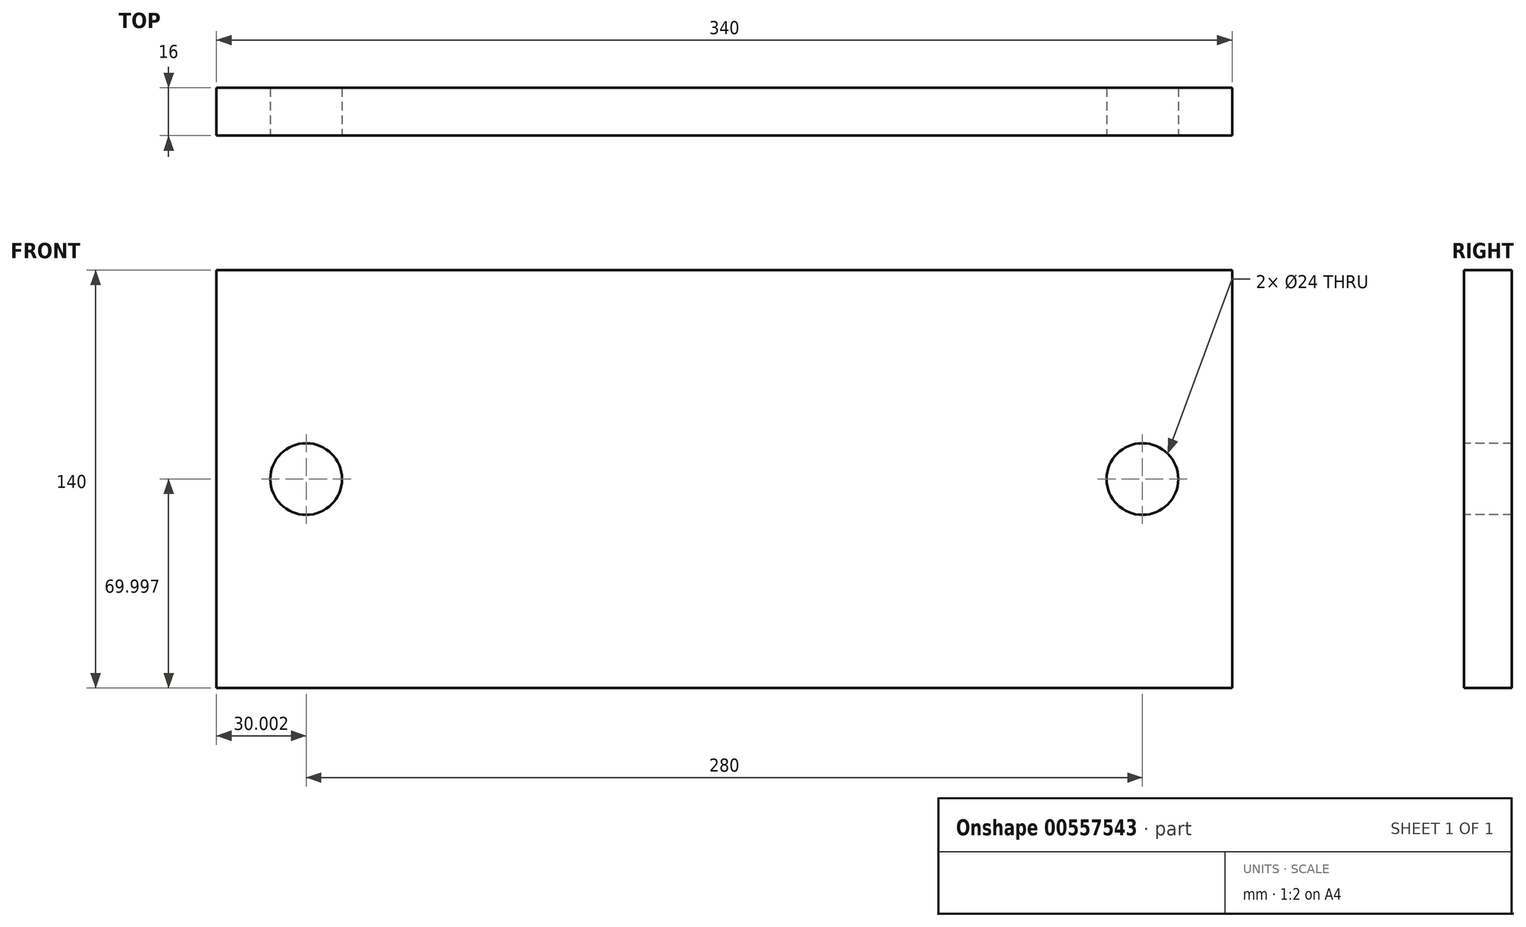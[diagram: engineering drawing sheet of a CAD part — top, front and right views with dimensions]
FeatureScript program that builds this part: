
annotation { "Feature Type Name" : "Feature", "Feature Type Description" : "" }
export const myFeature = defineFeature(function(context is Context, id is Id, definition is map)
    precondition{}
    {
        {
            var Q0;
            Q0=qCreatedBy(makeId("Front.planeOp"),FACE);
            var sketch = newSketch(context, id + "F0", { "sketchPlane" : qUnion([Q0])});
            skLineSegment(sketch, "E0.bottom", {"start": v(-47.63, -28.44) * mm, "end": v(292.37, -28.44) * mm});
            skLineSegment(sketch, "E0.top", {"start": v(-47.63, 111.56) * mm, "end": v(292.37, 111.56) * mm});
            skLineSegment(sketch, "E0.left", {"start": v(-47.63, -28.44) * mm, "end": v(-47.63, 111.56) * mm});
            skLineSegment(sketch, "E0.right", {"start": v(292.37, -28.44) * mm, "end": v(292.37, 111.56) * mm});
            skSolve(sketch);
        }
        {
            var Q0;
            Q0 = qSketchRegion(id + "F0", true);
            extrude(context, id + "F1", {"entities" : qUnion([Q0]), "depth" : 16 * mm, "offsetDistance" : 25 * mm});
        }
        {
            var Q0;
            Q0=makeQuery(id+"F1.opExtrude","CAP_FACE",FACE,{"disambiguationData":[OSD([sQuery(id+"F0.wireOp",EDGE,"E0.bottom"),sQuery(id+"F0.wireOp",EDGE,"E0.top"),sQuery(id+"F0.wireOp",EDGE,"E0.left"),sQuery(id+"F0.wireOp",EDGE,"E0.right")])],"isStart":false});
            var sketch = newSketch(context, id + "F2", { "sketchPlane" : qUnion([Q0])});
            skPoint(sketch, "E1.endSnap0", {"position": v(292.37, 41.56) * mm});
            skCircle(sketch, "E2", {"center": v(-17.63, 41.56) * mm, "radius": 12 * mm});
            skCircle(sketch, "E3", {"center": v(262.37, 41.56) * mm, "radius": 12 * mm});
            skSolve(sketch);
        }
        {
            var Q0;
            Q0 = qSketchRegion(id + "F2", true);
            extrude(context, id + "F3", {"entities" : qUnion([Q0]), "operationType" : NewBodyOperationType.REMOVE, "oppositeDirection" : true, "depth" : 16 * mm, "offsetDistance" : 25 * mm});
        }
    });
